# Revit family: Kessel 851501 en
name_source: partatom
category: Sanitärinstallationen
revit_build: Autodesk Revit 2017 (Build: 20160225_1515(x64)
units: mm (PartAtom-declared; Revit-internal decimal feet)

## family parameters
Arbeitsebenenbasiert = Nein
Beim Laden mit Abzugskörper schneiden = Nein
Bemaßung runder Anschluss = Durchmesser verwenden
Gemeinsam genutzt = Nein
Immer vertikal = Ja
Raumberechnungspunkt = Nein
Teiletyp = Normal

## types (1)
- Kessel 851501 en
    <1.010.00.2> Number of the part of the guideline = 38
    <1.010.00.3> Issue date (month) of the guideline = 201805
    <1.010.00.4> Manufacturer name = Kessel
    <1.010.00.5> Revision date of the file = 20190228
    <1.800.00.3> BS number = 100014000000000000000000000003000000???00000000005???00001
    <1.800.00.4> Comment field = Rückstau-Technikmodul Controlfix DN 150, geschl. Durchgangsgerinne
    <1.810.00.3> Manufacturer’s reference number = 851501
    <1.810.00.4> DATANORM number = 851501
    <1.960/3L.00.8> Link (URL) = http://www.kessel.de
    <38.100.00.4> Drain type for floor, roof and sanitary objects = Rückstauverschlüsse
    <38.110.00.4> Floor, roof and sanitary works sequences = Rückstau-Technikmodul Controlfix
    <38.400.00.3> Material of the drain body = Kunststoff
    <38.700.00.15> Connection to GLT, GA = no
    <38.700.00.16> Fire resistance class can be retrofitted = no
    <38.700.00.4> product name = Rückstau-Technikmodul Controlfix DN 150, geschl. Durchgangsgerinne
    <38.700.00.6> Complete article (one-piece) from combination (multi-part design) Drain body and attachment piece = yes
    <38.700.00.7> Potential compensation (ground connection) available = no
    <38.700.00.8> Electrical connection = no
    <38.710.01.10> depth [mm] = 1200
    <38.710.01.11> installation height [mm] = 520
    <38.710.01.14> with sound decoupling = no
    <38.710.01.15> Leafy / Kiefang = no
    <38.710.01.3> Product name = Rückstau-Technikmodul Controlfix DN 100, geschl. Durchgangsgerinne
    <38.710.13.3> Product name = Rückstau-Technikmodul Controlfix DN 100, geschl. Durchgangsgerinne
    <38.710.13.4> Variant of the drainage drain = point drain
    <38.710.13.7> Leafy / Kiefang = no
    <38.710.16.3> Type of measurements = external dimensions
    <38.710.16.5> Width = 1200
    <38.710.16.6> Height = 520
    <38.710.16.7> Mass (net) = 79
    CONNECTOR0_DIAMETER_dX_0r = 0 mm  [stored 0 ft]
    CONNECTOR0_dX_00 = 747 mm
    CONNECTOR0_dX_01 = 732 mm
    CONNECTOR0_ref_dX = 732 mm
    CONNECTOR0_ref_dZ = 277 mm  [stored 0.908793 ft]
    CONNECTOR1_DIAMETER_dX_0r = 0 mm  [stored 0 ft]
    CONNECTOR1_dX_00 = 126 mm
    CONNECTOR1_dX_01 = 131 mm
    CONNECTOR1_ref_dX = 126 mm
    CONNECTOR1_ref_dY = 34 mm
    CONNECTOR1_ref_dZ = 420 mm
    CONNECTOR2_DIAMETER_dX_0r = 0 mm  [stored 0 ft]
    CONNECTOR2_dX_00 = 126 mm
    CONNECTOR2_dX_01 = 131 mm
    CONNECTOR2_ref_dX = 126 mm
    CONNECTOR2_ref_dY = 34 mm
    CONNECTOR2_ref_dZ = 396 mm
    CONNECTOR3_DIAMETER_dX_0r = 0 mm  [stored 0 ft]
    CONNECTOR3_dX_00 = 126 mm
    CONNECTOR3_dX_01 = 131 mm
    CONNECTOR3_ref_dX = 126 mm
    CONNECTOR3_ref_dY = 46 mm  [stored 0.150919 ft]
    CONNECTOR3_ref_dZ = 408 mm
    CONNECTOR4_DIAMETER_dX_0r = 0 mm  [stored 0 ft]
    CONNECTOR4_dX_00 = 126 mm
    CONNECTOR4_dX_01 = 131 mm
    CONNECTOR4_ref_dX = 126 mm
    CONNECTOR4_ref_dY = 22 mm  [stored 0.0721785 ft]
    CONNECTOR4_ref_dZ = 408 mm
    CONNECTOR5_DIAMETER_dX_0r = 0 mm  [stored 0 ft]
    CONNECTOR5_dX_00 = 635 mm
    CONNECTOR5_dX_01 = 726 mm
    CONNECTOR5_ref_dX = 635 mm
    CONNECTOR5_ref_dZ = 267 mm  [stored 0.875984 ft]
    Hersteller = Kessel
    Modell = 851501
    URL = www.kessel.de

note: [stored X ft] marks values corroborated as IEEE doubles in the binary element streams (Revit-internal decimal feet)

## geometry (parser evidence)
native form markers: Sweep x2
no freeform markers — native parametric forms only
